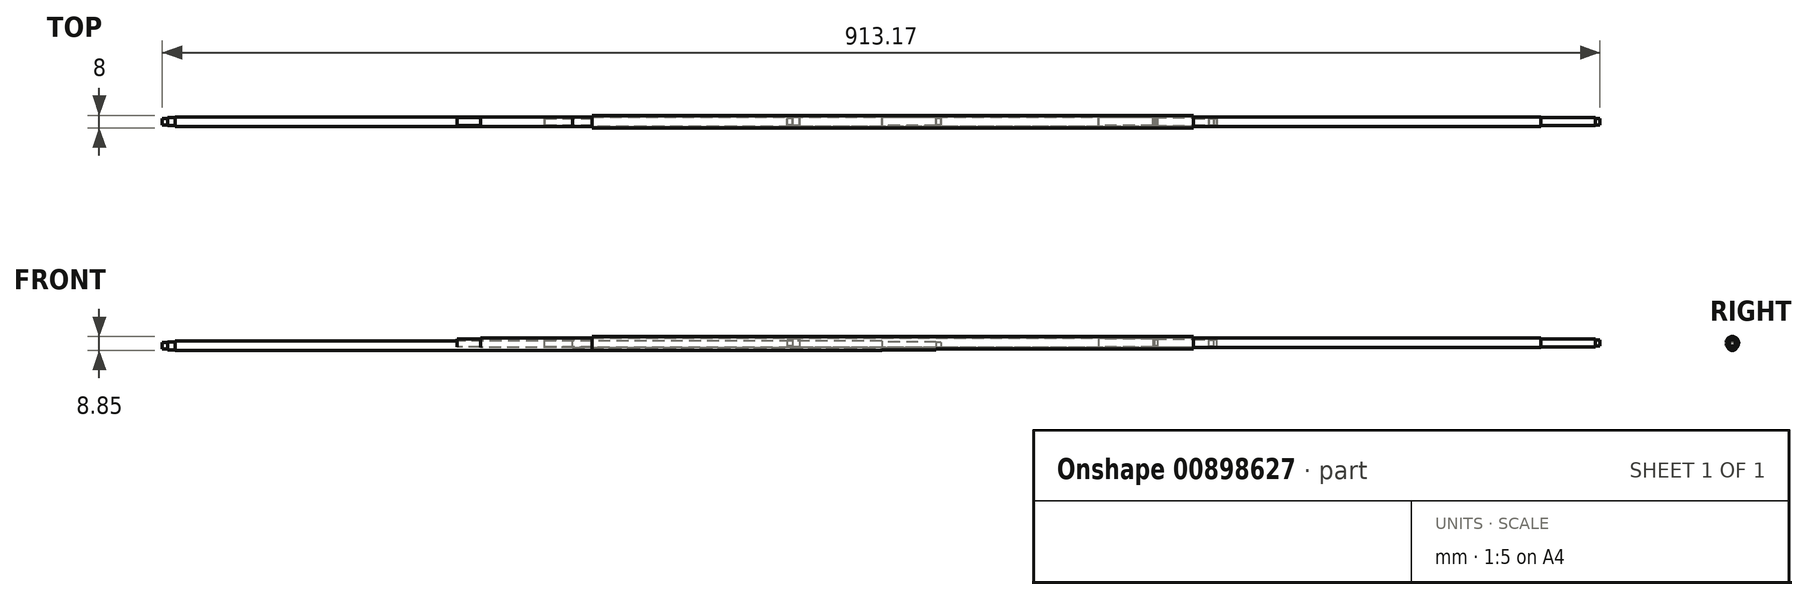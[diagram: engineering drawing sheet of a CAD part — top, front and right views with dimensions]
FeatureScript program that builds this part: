
annotation { "Feature Type Name" : "Feature", "Feature Type Description" : "" }
export const myFeature = defineFeature(function(context is Context, id is Id, definition is map)
    precondition{}
    {
        {
            var Q0;
            Q0=qCreatedBy(makeId("Front.planeOp"),FACE);
            var sketch = newSketch(context, id + "F0", { "sketchPlane" : qUnion([Q0])});
            skLineSegment(sketch, "E0", {"start": v(-55.75, 0) * mm, "end": v(-55.75, 2.5) * mm});
            skLineSegment(sketch, "E1", {"start": v(-55.75, 2.5) * mm, "end": v(-40.75, 2.5) * mm});
            skLineSegment(sketch, "E2", {"start": v(-40.75, 2.5) * mm, "end": v(-40.75, 3) * mm});
            skLineSegment(sketch, "E3", {"start": v(-40.75, 3) * mm, "end": v(351.75, 3) * mm});
            skLineSegment(sketch, "E4", {"start": v(351.75, 3) * mm, "end": v(351.75, 2.5) * mm});
            skLineSegment(sketch, "E5", {"start": v(351.75, 2.5) * mm, "end": v(386.25, 2.5) * mm});
            skLineSegment(sketch, "E6", {"start": v(386.25, 2) * mm, "end": v(389.25, 2) * mm});
            skLineSegment(sketch, "E7", {"start": v(389.25, 2) * mm, "end": v(389.25, 0) * mm});
            skLineSegment(sketch, "E8", {"start": v(-105.17, 0) * mm, "end": v(438.03, 0) * mm, "construction": true});
            skLineSegment(sketch, "E9", {"start": v(386.25, 2.5) * mm, "end": v(386.25, 2) * mm});
            skLineSegment(sketch, "E10", {"start": v(389.25, 0) * mm, "end": v(-55.75, 0) * mm});
            skSolve(sketch);
        }
        {
            var Q0;
            Q0=qSketchRegion(id+"F0",true);
            var Q1;
            Q1=sQuery(id+"F0.wireOp",EDGE,"E8");
            revolve(context, id + "F1", {"entities" : qUnion([Q0]), "axis" : qUnion([Q1]), "revolveType" : RevolveType.FULL});
        }
        {
            var Q0;
            Q0=qCreatedBy(makeId("Front.planeOp"),FACE);
            var sketch = newSketch(context, id + "F2", { "sketchPlane" : qUnion([Q0])});
            skLineSegment(sketch, "E11", {"start": v(-22.49, 0) * mm, "end": v(33.28, 0) * mm, "construction": true});
            skLineSegment(sketch, "E12", {"start": v(153.84, 0) * mm, "end": v(153.84, 2) * mm});
            skLineSegment(sketch, "E13", {"start": v(153.84, 2) * mm, "end": v(157.34, 2) * mm});
            skLineSegment(sketch, "E14", {"start": v(667.34, 2) * mm, "end": v(670.34, 2) * mm});
            skLineSegment(sketch, "E15", {"start": v(670.34, 2) * mm, "end": v(670.34, 0) * mm});
            skLineSegment(sketch, "E16", {"start": v(153.84, 0) * mm, "end": v(670.34, 0) * mm});
            skLineSegment(sketch, "E17", {"start": v(632.84, 3) * mm, "end": v(632.84, 2.5) * mm});
            skLineSegment(sketch, "E18", {"start": v(632.84, 2.5) * mm, "end": v(667.34, 2.5) * mm});
            skLineSegment(sketch, "E19", {"start": v(667.34, 2.5) * mm, "end": v(667.34, 2) * mm});
            skLineSegment(sketch, "E20", {"start": v(157.34, 2.5) * mm, "end": v(161.84, 2.5) * mm});
            skLineSegment(sketch, "E21", {"start": v(161.84, 2.5) * mm, "end": v(161.84, 3) * mm});
            skLineSegment(sketch, "E22", {"start": v(157.34, 2.5) * mm, "end": v(157.34, 2) * mm});
            skLineSegment(sketch, "E23", {"start": v(161.84, 3) * mm, "end": v(632.84, 3) * mm});
            skSolve(sketch);
        }
        {
            var Q0;
            Q0=qSketchRegion(id+"F2",true);
            var Q1;
            Q1=sQuery(id+"F2.wireOp",EDGE,"E16");
            revolve(context, id + "F3", {"entities" : qUnion([Q0]), "axis" : qUnion([Q1]), "revolveType" : RevolveType.FULL});
        }
        {
            var Q0;
            Q0=qCreatedBy(makeId("Front.planeOp"),FACE);
            var sketch = newSketch(context, id + "F4", { "sketchPlane" : qUnion([Q0])});
            skLineSegment(sketch, "E24", {"start": v(0, 0) * mm, "end": v(0, 2.5) * mm});
            skLineSegment(sketch, "E25", {"start": v(0, 2.5) * mm, "end": v(17.7, 2.5) * mm});
            skLineSegment(sketch, "E26", {"start": v(17.7, 2.5) * mm, "end": v(17.7, 3) * mm});
            skLineSegment(sketch, "E27", {"start": v(17.7, 3) * mm, "end": v(387.5, 3) * mm});
            skLineSegment(sketch, "E28", {"start": v(387.5, 3) * mm, "end": v(387.5, 2.5) * mm});
            skLineSegment(sketch, "E29", {"start": v(387.5, 2.5) * mm, "end": v(422, 2.5) * mm});
            skLineSegment(sketch, "E30", {"start": v(-63.17, 0) * mm, "end": v(-96, 0) * mm, "construction": true});
            skLineSegment(sketch, "E31", {"start": v(422, 2.5) * mm, "end": v(422, 2) * mm});
            skLineSegment(sketch, "E32", {"start": v(422, 2) * mm, "end": v(425, 2) * mm});
            skLineSegment(sketch, "E33", {"start": v(425, 2) * mm, "end": v(425, 0) * mm});
            skLineSegment(sketch, "E34", {"start": v(0, 0) * mm, "end": v(425, 0) * mm});
            skSolve(sketch);
        }
        {
            var Q0;
            Q0=qSketchRegion(id+"F4",true);
            var Q1;
            Q1=sQuery(id+"F4.wireOp",EDGE,"E30");
            revolve(context, id + "F5", {"entities" : qUnion([Q0]), "axis" : qUnion([Q1]), "revolveType" : RevolveType.FULL});
        }
        {
            var Q0;
            Q0=qCreatedBy(makeId("Front.planeOp"),FACE);
            var sketch = newSketch(context, id + "F6", { "sketchPlane" : qUnion([Q0])});
            skLineSegment(sketch, "E35", {"start": v(-233.88, -1.85) * mm, "end": v(-178.1, -1.85) * mm, "construction": true});
            skLineSegment(sketch, "E36", {"start": v(-242.83, -1.85) * mm, "end": v(-242.83, 0.15) * mm});
            skLineSegment(sketch, "E37", {"start": v(-242.83, 0.15) * mm, "end": v(-239.33, 0.15) * mm});
            skLineSegment(sketch, "E38", {"start": v(-239.33, 0.15) * mm, "end": v(-239.33, 0.65) * mm});
            skLineSegment(sketch, "E39", {"start": v(-239.33, 0.65) * mm, "end": v(-234.83, 0.65) * mm});
            skLineSegment(sketch, "E40", {"start": v(-234.83, 0.65) * mm, "end": v(-234.83, 1.15) * mm});
            skLineSegment(sketch, "E41", {"start": v(-234.83, 1.15) * mm, "end": v(214.17, 1.15) * mm});
            skLineSegment(sketch, "E42", {"start": v(214.17, 1.15) * mm, "end": v(214.17, 0.65) * mm});
            skLineSegment(sketch, "E43", {"start": v(214.17, 0.65) * mm, "end": v(248.67, 0.65) * mm});
            skLineSegment(sketch, "E44", {"start": v(248.67, 0.65) * mm, "end": v(248.67, 0.15) * mm});
            skLineSegment(sketch, "E45", {"start": v(248.67, 0.15) * mm, "end": v(251.67, 0.15) * mm});
            skLineSegment(sketch, "E46", {"start": v(251.67, 0.15) * mm, "end": v(251.67, -1.85) * mm});
            skLineSegment(sketch, "E47", {"start": v(-242.83, -1.85) * mm, "end": v(251.67, -1.85) * mm});
            skSolve(sketch);
        }
        {
            var Q0;
            Q0=qSketchRegion(id+"F6",true);
            var Q1;
            Q1=sQuery(id+"F6.wireOp",EDGE,"E47");
            revolve(context, id + "F7", {"entities" : qUnion([Q0]), "axis" : qUnion([Q1]), "revolveType" : RevolveType.FULL});
        }
        {
            var Q0;
            Q0=qCreatedBy(makeId("Front.planeOp"),FACE);
            var sketch = newSketch(context, id + "F8", { "sketchPlane" : qUnion([Q0])});
            skLineSegment(sketch, "E48", {"start": v(0, 0) * mm, "end": v(0, 2.15) * mm});
            skLineSegment(sketch, "E49", {"start": v(0, 2.15) * mm, "end": v(30, 2.15) * mm});
            skLineSegment(sketch, "E50", {"start": v(30, 2.15) * mm, "end": v(30, 4) * mm});
            skLineSegment(sketch, "E51", {"start": v(30, 4) * mm, "end": v(412, 4) * mm});
            skLineSegment(sketch, "E52", {"start": v(412, 4) * mm, "end": v(412, 2.15) * mm});
            skLineSegment(sketch, "E53", {"start": v(412, 2.15) * mm, "end": v(427, 2.15) * mm});
            skLineSegment(sketch, "E54", {"start": v(427, 2.15) * mm, "end": v(427, 0) * mm});
            skLineSegment(sketch, "E55", {"start": v(427, 0) * mm, "end": v(0, 0) * mm});
            skSolve(sketch);
        }
        {
            var Q0;
            Q0=qSketchRegion(id+"F8",true);
            var Q1;
            Q1=sQuery(id+"F8.wireOp",EDGE,"E55");
            revolve(context, id + "F9", {"entities" : qUnion([Q0]), "axis" : qUnion([Q1]), "revolveType" : RevolveType.FULL});
        }
    });
